# Revit family: HLM-S2-32600-840-SI-DA-SEN
name_source: partatom
category: Oprawy oświetleniowe
revit_build: Autodesk Revit 2017 (Build: 20190507_1515(x64)
units: mm (PartAtom-declared; Revit-internal decimal feet)

## family parameters
Numer OmniClass = 23.80.70.11
Obiekt nadrzędny = Powierzchnia
Punkt obliczania pomieszczeń = Nie
Tnij formami wycięć po wczytaniu = Nie
Typ części = Normalny
Tytuł OmniClass = Luminaries for Internal Lighting
Współdzielony = Nie
Wymiar okrągłego złącza = Użyj średnicy
Źródło światła = Tak

## types (1)
- HLM-S2-32600-840-SI-DA-SEN
    Domyślna rzędna = 0 mm  [stored 0 ft]
    Emituj kształt widoczny w renderingu = Nie
    Emituj z długości prostokąta = 363 mm  [stored 1.19094 ft]
    Emituj z szerokości prostokąta = 1015 mm  [stored 3.33005 ft]
    Filtr koloru = 16777215
    Kod zespołu = D5020200
    Lampa = LED
    Model = SPY0630005SI
    Obciążenie pozorne = 212 VA
    Odchylenie kierunku = 90.00°
    Plik sieci fotometrycznej = HLM-S 16300840 SI-DA-2SC.IES
    Producent = RIDI Leuchten GmbH
    URL = www.spectral.de
    Zmiana temperatury barwowej przyciemniania lampy = <Brak>
    brand = Spectral
    conformity mark = CE
    electrical safety class = 1
    height = 1947 mm  [stored 6.3878 ft]
    ingress protection (IP) code = IP20
    length = 924 mm  [stored 3.0315 ft]
    nominal frequency = 50-60Hz
    nominal voltage = 230
    product name = HLM-S2 32600/840 SI-DA-SEN
    rated input power = 212
    voltage type (AC, DC, UC) = AC
    weight = 34 kg
    width = 380 mm

note: [stored X ft] marks values corroborated as IEEE doubles in the binary element streams (Revit-internal decimal feet)
